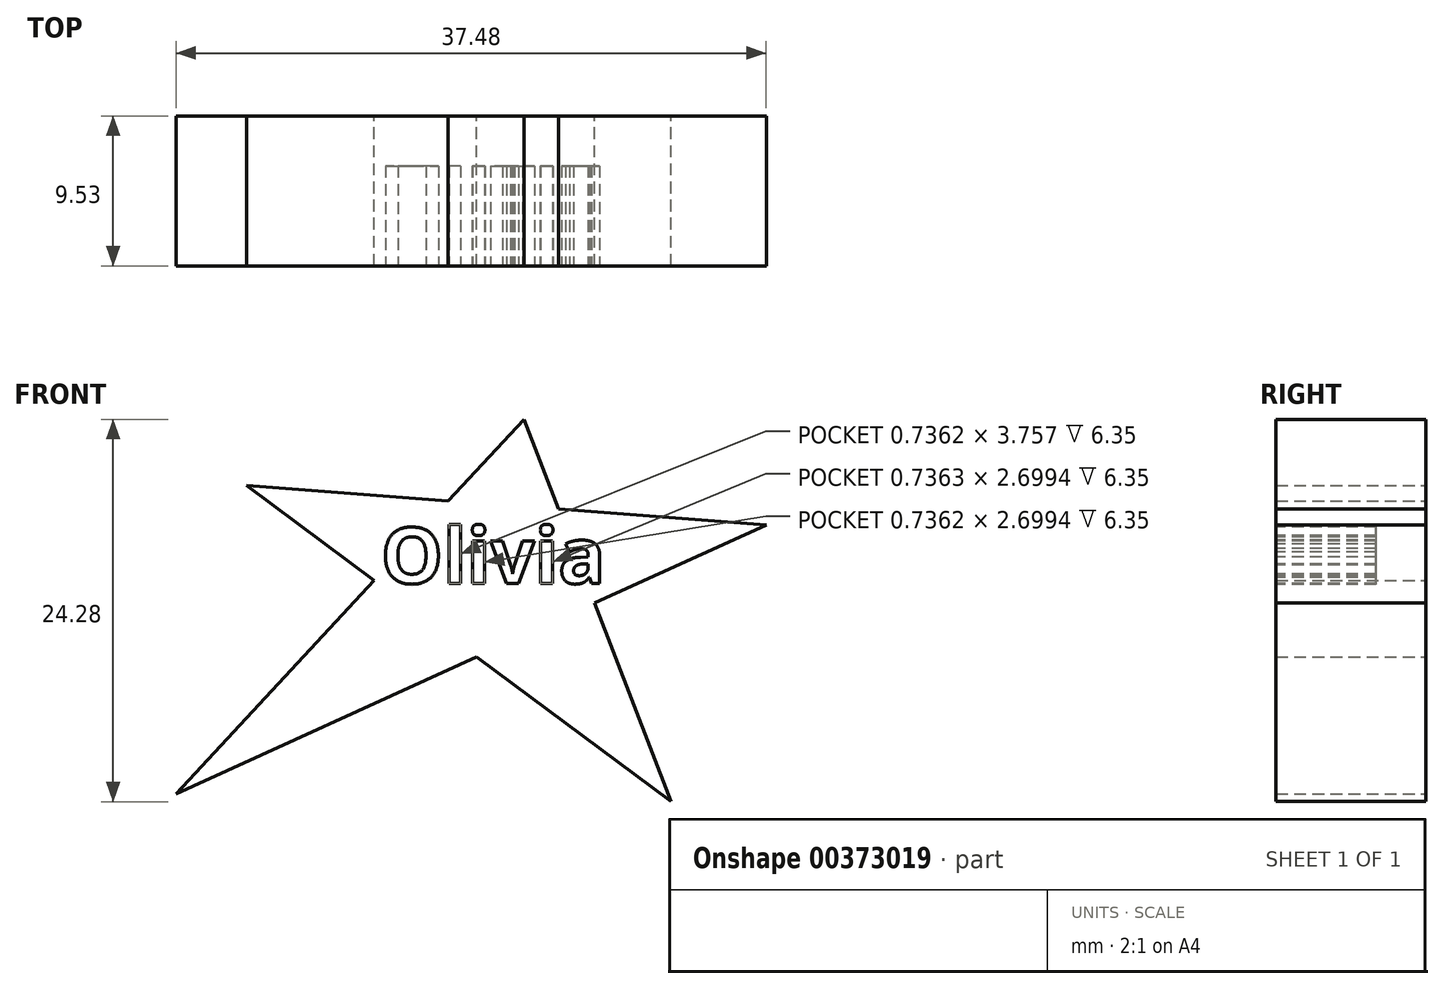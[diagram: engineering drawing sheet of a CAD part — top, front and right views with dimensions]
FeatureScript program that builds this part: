
annotation { "Feature Type Name" : "Feature", "Feature Type Description" : "" }
export const myFeature = defineFeature(function(context is Context, id is Id, definition is map)
    precondition{}
    {
        {
            var Q0;
            Q0=qCreatedBy(makeId("Front.planeOp"),FACE);
            var sketch = newSketch(context, id + "F0", { "sketchPlane" : qUnion([Q0])});
            skLineSegment(sketch, "E0", {"start": v(-51.61, 30.5) * mm, "end": v(-39.03, 44.04) * mm});
            skLineSegment(sketch, "E1", {"start": v(-29.51, 54.27) * mm, "end": v(-27.32, 48.56) * mm});
            skLineSegment(sketch, "E2", {"start": v(-19.72, 29.65) * mm, "end": v(-32.52, 39.19) * mm});
            skLineSegment(sketch, "E3", {"start": v(-47.14, 50.08) * mm, "end": v(-34.32, 49.1) * mm});
            skLineSegment(sketch, "E4", {"start": v(-14.13, 47.56) * mm, "end": v(-25.02, 42.6) * mm});
            skLineSegment(sketch, "E5.trimOffspring", {"start": v(-34.32, 49.1) * mm, "end": v(-29.51, 54.27) * mm});
            skLineSegment(sketch, "E6.trimOffspring", {"start": v(-27.32, 48.56) * mm, "end": v(-14.13, 47.56) * mm});
            skLineSegment(sketch, "E7.trimOffspring", {"start": v(-32.52, 39.19) * mm, "end": v(-51.61, 30.5) * mm});
            skLineSegment(sketch, "E8.trimOffspring", {"start": v(-39.03, 44.04) * mm, "end": v(-47.14, 50.08) * mm});
            skLineSegment(sketch, "E9.trimOffspring", {"start": v(-25.02, 42.6) * mm, "end": v(-19.72, 28.81) * mm});
            skSolve(sketch);
        }
        {
            var Q0;
            Q0=makeQuery(id+"F0.imprint","IMPRINT",FACE,{"disambiguationData":[TD([[makeQuery(id+"F0.imprint","IMPRINT",EDGE,{"derivedFrom":sQuery(id+"F0.wireOp",EDGE,"E0")}),-1.0]])]});
            extrude(context, id + "F1", {"entities" : qUnion([Q0]), "depth" : 9.52 * mm});
        }
        {
            var Q0;
            Q0=makeQuery(id+"F1.opExtrude","CAP_FACE",FACE,{"disambiguationData":[OSD([sQuery(id+"F0.wireOp",EDGE,"E0"),sQuery(id+"F0.wireOp",EDGE,"E1"),sQuery(id+"F0.wireOp",EDGE,"E2"),sQuery(id+"F0.wireOp",EDGE,"E3"),sQuery(id+"F0.wireOp",EDGE,"E4"),sQuery(id+"F0.wireOp",EDGE,"E5.trimOffspring"),sQuery(id+"F0.wireOp",EDGE,"E6.trimOffspring"),sQuery(id+"F0.wireOp",EDGE,"E7.trimOffspring"),sQuery(id+"F0.wireOp",EDGE,"E8.trimOffspring"),sQuery(id+"F0.wireOp",EDGE,"E9.trimOffspring")])],"isStart":false});
            var sketch = newSketch(context, id + "F2", { "sketchPlane" : qUnion([Q0])});
            skText(sketch, "E10", { "text": "Olivia", "fontName": "OpenSans-Bold.ttf"});
            const initialGuessF2  = {"E10": [-0.0386, 0.04385, 1, 0, 0.00356]};
            skSetInitialGuess(sketch, initialGuessF2);
            skSolve(sketch);
        }
        {
            var Q0;
            Q0 = qSketchRegion(id + "F2", true);
            extrude(context, id + "F3", {"entities" : qUnion([Q0]), "operationType" : NewBodyOperationType.REMOVE, "oppositeDirection" : true, "depth" : 6.35 * mm});
        }
    });
